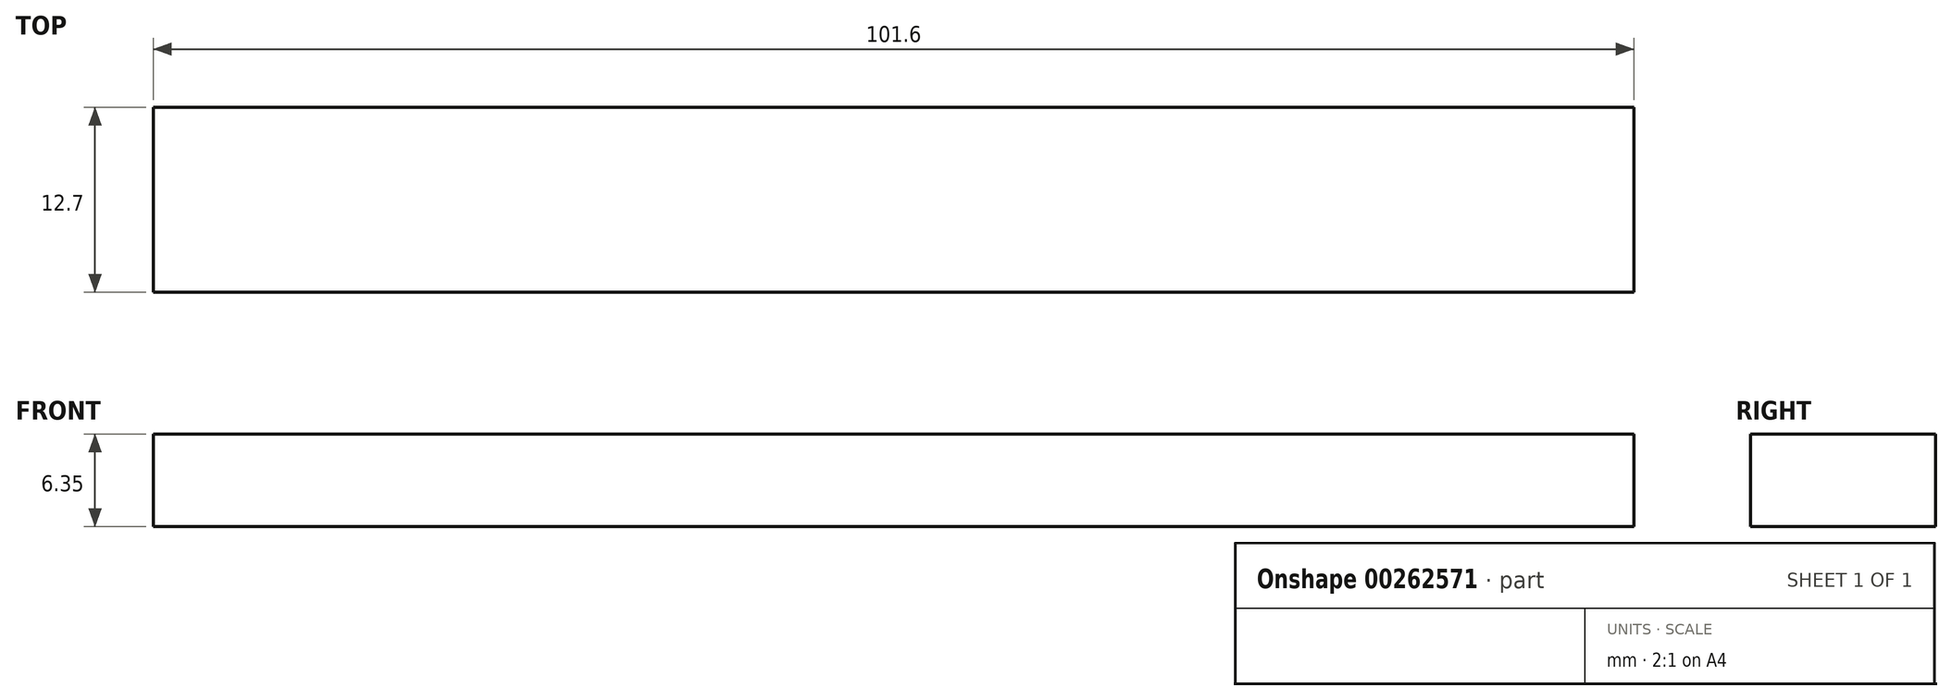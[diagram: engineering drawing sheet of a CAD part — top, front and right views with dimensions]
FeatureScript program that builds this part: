
annotation { "Feature Type Name" : "Feature", "Feature Type Description" : "" }
export const myFeature = defineFeature(function(context is Context, id is Id, definition is map)
    precondition{}
    {
        {
            var Q0;
            Q0=qCreatedBy(makeId("Top.planeOp"),FACE);
            var sketch = newSketch(context, id + "F0", { "sketchPlane" : qUnion([Q0])});
            skLineSegment(sketch, "E0.bottom", {"start": v(0, 0) * mm, "end": v(101.6, 0) * mm});
            skLineSegment(sketch, "E0.top", {"start": v(0, -12.7) * mm, "end": v(101.6, -12.7) * mm});
            skLineSegment(sketch, "E0.left", {"start": v(0, 0) * mm, "end": v(0, -12.7) * mm});
            skLineSegment(sketch, "E0.right", {"start": v(101.6, 0) * mm, "end": v(101.6, -12.7) * mm});
            skSolve(sketch);
        }
        {
            var Q0;
            Q0=makeQuery(id+"F0.imprint","IMPRINT",FACE,{"disambiguationData":[TD([[makeQuery(id+"F0.imprint","IMPRINT",EDGE,{"derivedFrom":sQuery(id+"F0.wireOp",EDGE,"E0.bottom")}),-1.0]])]});
            extrude(context, id + "F1", {"entities" : qUnion([Q0]), "depth" : 6.35 * mm});
        }
    });
